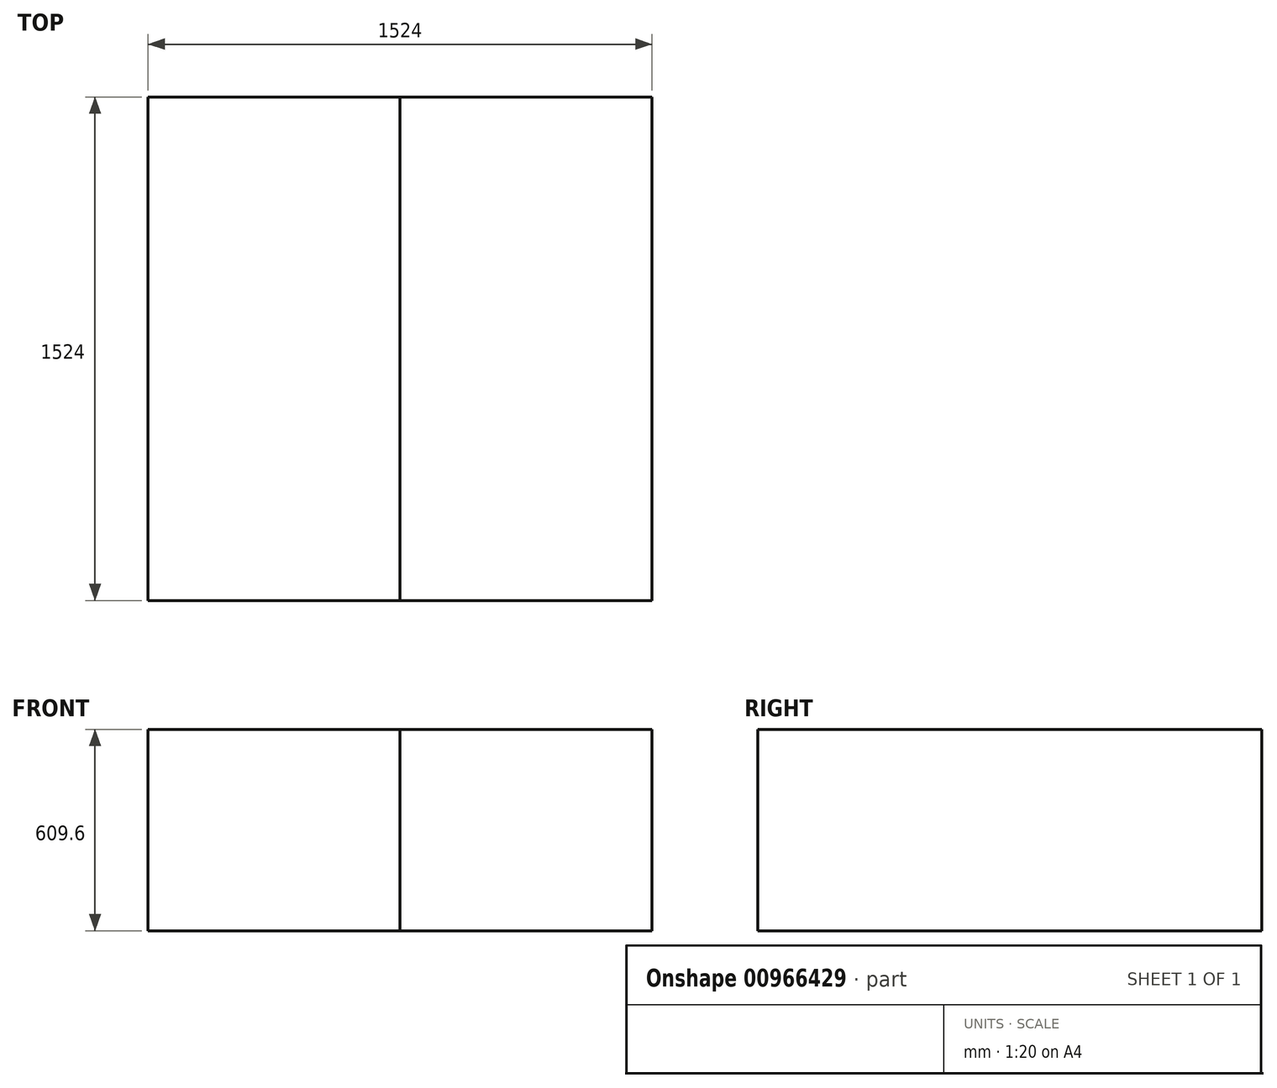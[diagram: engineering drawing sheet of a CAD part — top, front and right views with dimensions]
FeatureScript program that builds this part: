
annotation { "Feature Type Name" : "Feature", "Feature Type Description" : "" }
export const myFeature = defineFeature(function(context is Context, id is Id, definition is map)
    precondition{}
    {
        {
            var Q0;
            Q0=qCreatedBy(makeId("Right.planeOp"),FACE);
            var sketch = newSketch(context, id + "F0", { "sketchPlane" : qUnion([Q0])});
            skLineSegment(sketch, "E0.bottom", {"start": v(0, 0) * mm, "end": v(1524, 0) * mm});
            skLineSegment(sketch, "E0.top", {"start": v(0, 609.6) * mm, "end": v(1524, 609.6) * mm});
            skLineSegment(sketch, "E0.left", {"start": v(0, 0) * mm, "end": v(0, 609.6) * mm});
            skLineSegment(sketch, "E0.right", {"start": v(1524, 0) * mm, "end": v(1524, 609.6) * mm});
            skSolve(sketch);
        }
        {
            var Q0;
            Q0=makeQuery(id+"F0.imprint","IMPRINT",FACE,{"disambiguationData":[TD([[makeQuery(id+"F0.imprint","IMPRINT",EDGE,{"derivedFrom":sQuery(id+"F0.wireOp",EDGE,"E0.bottom")}),1.0]])]});
            extrude(context, id + "F1", {"entities" : qUnion([Q0]), "depth" : 762 * mm, "offsetDistance" : 25.4 * mm});
        }
        {
            var Q0;
            Q0=makeQuery(id+"F1.opExtrude","SWEPT_BODY",BODY,{"disambiguationData":[OSD([sQuery(id+"F0.wireOp",EDGE,"E0.bottom"),sQuery(id+"F0.wireOp",EDGE,"E0.top"),sQuery(id+"F0.wireOp",EDGE,"E0.left"),sQuery(id+"F0.wireOp",EDGE,"E0.right")])]});
            var Q1;
            Q1=qCreatedBy(makeId("Right.planeOp"),FACE);
            mirror(context, id + "F2", {"entities" : qUnion([Q0]), "mirrorPlane" : qUnion([Q1])});
        }
    });
